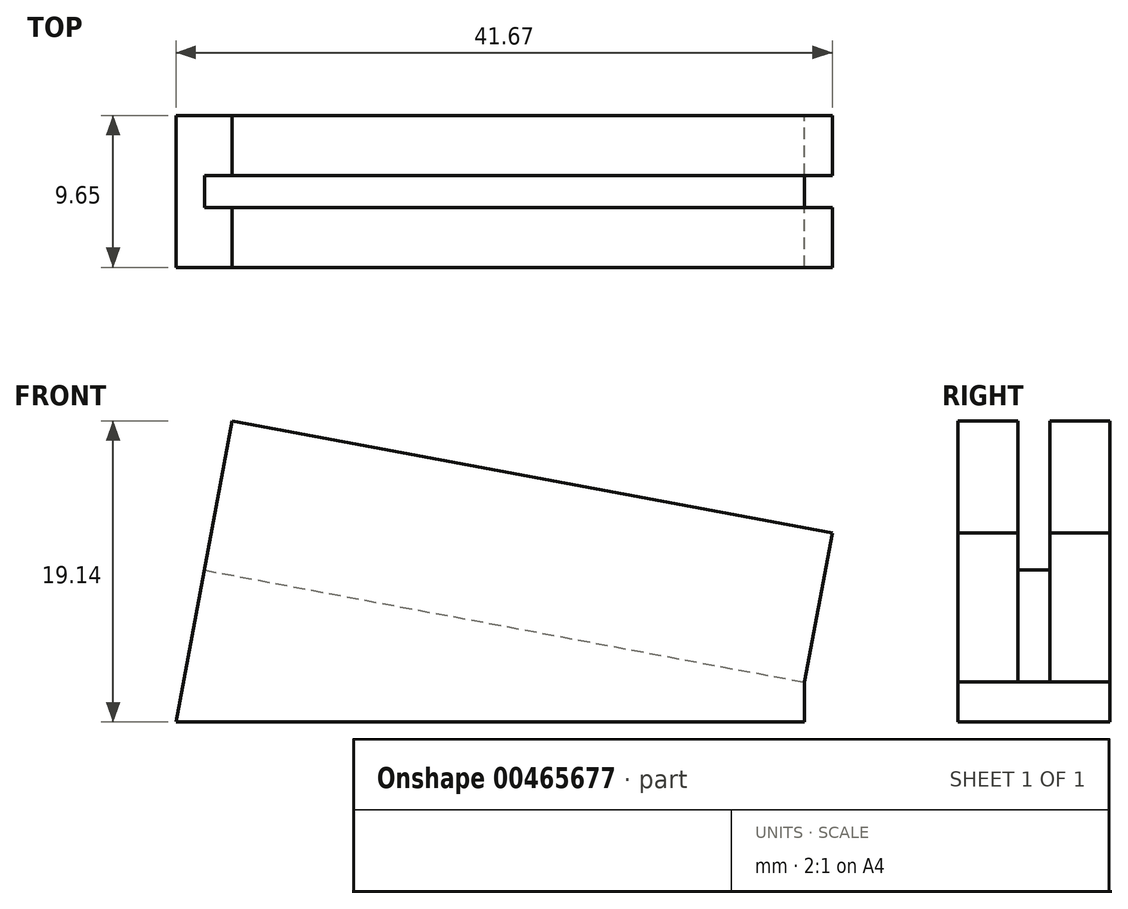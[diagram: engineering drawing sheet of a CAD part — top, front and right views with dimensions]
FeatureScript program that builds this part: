
annotation { "Feature Type Name" : "Feature", "Feature Type Description" : "" }
export const myFeature = defineFeature(function(context is Context, id is Id, definition is map)
    precondition{}
    {
        {
            var Q0;
            Q0=qCreatedBy(makeId("Front.planeOp"),FACE);
            var sketch = newSketch(context, id + "F0", { "sketchPlane" : qUnion([Q0])});
            skLineSegment(sketch, "E0", {"start": v(0, 0) * mm, "end": v(38.1, 0) * mm});
            skLineSegment(sketch, "E1", {"start": v(38.1, 0) * mm, "end": v(38.1, 2.54) * mm});
            skLineSegment(sketch, "E2", {"start": v(38.1, 2.54) * mm, "end": v(0, 9.65) * mm});
            skLineSegment(sketch, "E3", {"start": v(0, 9.65) * mm, "end": v(0, 0) * mm});
            skSolve(sketch);
        }
        {
            var Q0;
            Q0 = qSketchRegion(id + "F0", true);
            extrude(context, id + "F1", {"entities" : qUnion([Q0]), "depth" : 9.65 * mm});
        }
        {
            var Q0;
            Q0=makeQuery(id+"F1.opExtrude","SWEPT_FACE",FACE,{"disambiguationData":[OSD([sQuery(id+"F0.wireOp",EDGE,"E2")])]});
            var sketch = newSketch(context, id + "F2", { "sketchPlane" : qUnion([Q0])});
            skLineSegment(sketch, "E4.bottom", {"start": v(-1.77, -9.65) * mm, "end": v(36.99, -9.65) * mm});
            skLineSegment(sketch, "E4.top", {"start": v(-1.77, -5.84) * mm, "end": v(36.99, -5.84) * mm});
            skLineSegment(sketch, "E4.left", {"start": v(-1.77, -9.65) * mm, "end": v(-1.77, -5.84) * mm});
            skLineSegment(sketch, "E4.right", {"start": v(36.99, -9.65) * mm, "end": v(36.99, -5.84) * mm});
            skLineSegment(sketch, "E5.bottom", {"start": v(-1.77, 0) * mm, "end": v(36.99, 0) * mm});
            skLineSegment(sketch, "E5.top", {"start": v(-1.77, -3.81) * mm, "end": v(36.99, -3.81) * mm});
            skLineSegment(sketch, "E5.left", {"start": v(-1.77, 0) * mm, "end": v(-1.77, -3.81) * mm});
            skLineSegment(sketch, "E5.right", {"start": v(36.99, 0) * mm, "end": v(36.99, -3.81) * mm});
            skSolve(sketch);
        }
        {
            var Q0;
            Q0 = qSketchRegion(id + "F2", true);
            extrude(context, id + "F3", {"entities" : qUnion([Q0]), "operationType" : NewBodyOperationType.ADD, "depth" : 9.65 * mm});
        }
        {
            var Q0;
            Q0=makeQuery(id+"F3.boolean.opBoolean","MERGE",FACE,{"derivedFrom":[makeQuery(id+"F1.opExtrude","CAP_FACE",FACE,{"disambiguationData":[OSD([sQuery(id+"F0.wireOp",EDGE,"E0"),sQuery(id+"F0.wireOp",EDGE,"E1"),sQuery(id+"F0.wireOp",EDGE,"E2"),sQuery(id+"F0.wireOp",EDGE,"E3")])],"isStart":false}),makeQuery(id+"F3.opExtrude","SWEPT_FACE",FACE,{"disambiguationData":[OSD([sQuery(id+"F2.wireOp",EDGE,"E4.bottom")])]})]});
            var sketch = newSketch(context, id + "F4", { "sketchPlane" : qUnion([Q0])});
            skLineSegment(sketch, "E6", {"start": v(0, 9.65) * mm, "end": v(-1.8, 0) * mm});
            skLineSegment(sketch, "E7", {"start": v(-1.8, 0) * mm, "end": v(0, 0) * mm});
            skLineSegment(sketch, "E8", {"start": v(0, 0) * mm, "end": v(0, 9.65) * mm});
            skSolve(sketch);
        }
        {
            var Q0;
            Q0 = qSketchRegion(id + "F4", true);
            extrude(context, id + "F5", {"entities" : qUnion([Q0]), "operationType" : NewBodyOperationType.ADD, "oppositeDirection" : true, "depth" : 9.65 * mm});
        }
    });
